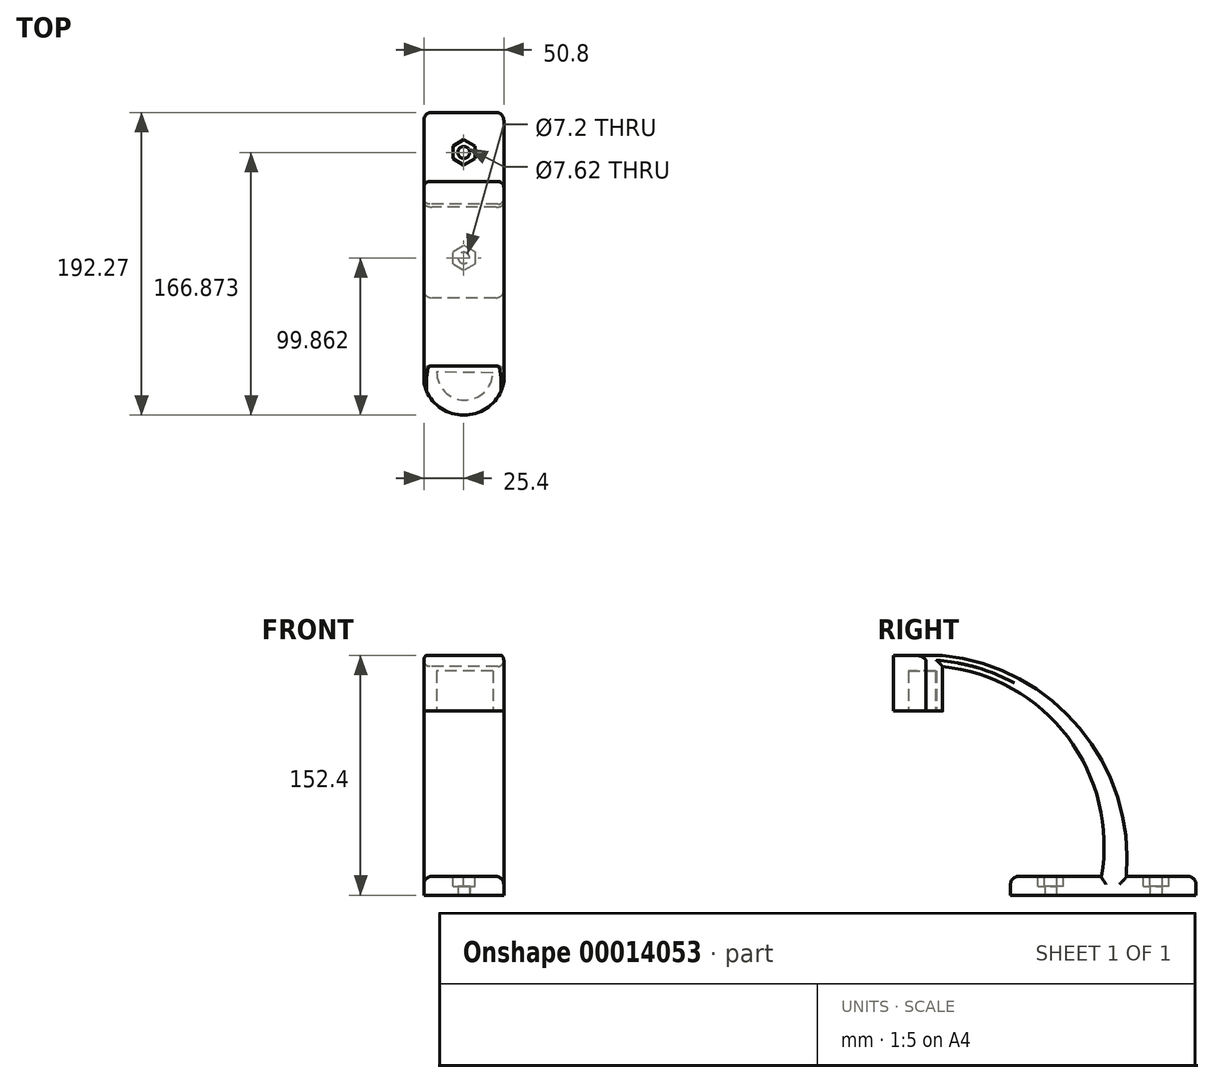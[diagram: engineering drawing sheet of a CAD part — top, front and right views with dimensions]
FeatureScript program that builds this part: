
annotation { "Feature Type Name" : "Feature", "Feature Type Description" : "" }
export const myFeature = defineFeature(function(context is Context, id is Id, definition is map)
    precondition{}
    {
        {
            var Q0;
            Q0=qCreatedBy(makeId("Right.planeOp"),FACE);
            var sketch = newSketch(context, id + "F0", { "sketchPlane" : qUnion([Q0])});
            skLineSegment(sketch, "E0.bottom", {"start": v(-57.77, 0) * mm, "end": v(60.04, 0) * mm});
            skLineSegment(sketch, "E0.top", {"start": v(-57.77, 11.91) * mm, "end": v(60.04, 11.91) * mm});
            skLineSegment(sketch, "E0.left", {"start": v(-57.77, 0) * mm, "end": v(-57.77, 11.91) * mm});
            skLineSegment(sketch, "E0.right", {"start": v(60.04, 0) * mm, "end": v(60.04, 11.91) * mm});
            skLineSegment(sketch, "E1.bottom", {"start": v(-132.44, 117) * mm, "end": v(-100.9, 117) * mm});
            skLineSegment(sketch, "E1.top", {"start": v(-132.44, 152.4) * mm, "end": v(-100.9, 152.4) * mm});
            skLineSegment(sketch, "E1.left", {"start": v(-132.44, 117) * mm, "end": v(-132.44, 152.4) * mm});
            skLineSegment(sketch, "E1.right", {"start": v(-100.9, 117) * mm, "end": v(-100.9, 152.4) * mm});
            skArc(sketch, "E2", {"start": v(15.8, 11.91) * mm, "mid": v(-13.86, 106) * mm, "end": v(-100.9, 152.4) * mm});
            skArc(sketch, "E3", {"start": v(0, 11.91) * mm, "mid": v(-21.52, 100.47) * mm, "end": v(-100.9, 145.2) * mm});
            skSolve(sketch);
        }
        {
            var Q0;
            Q0 = qSketchRegion(id + "F0", true);
            extrude(context, id + "F1", {"entities" : qUnion([Q0]), "depth" : 50.8 * mm});
        }
        {
            var Q0;
            Q0=makeQuery(id+"F1.opExtrude","SWEPT_FACE",FACE,{"disambiguationData":[OSD([sQuery(id+"F0.wireOp",EDGE,"E1.top")])]});
            var sketch = newSketch(context, id + "F2", { "sketchPlane" : qUnion([Q0])});
            skArc(sketch, "E4", {"start": v(0, -100.9) * mm, "mid": v(25.4, -132.23) * mm, "end": v(50.8, -100.9) * mm});
            skSolve(sketch);
        }
        {
            var Q0;
            {var subQ0=sQuery(id+"F0.wireOp",EDGE,"E1.top");var subQ4=makeQuery(id+"F1.opExtrude","SWEPT_EDGE",EDGE,{"disambiguationData":[OSD([subQ0,sQuery(id+"F0.wireOp",EDGE,"E1.left")])]});Q0=makeQuery(id+"F2.imprint","IMPRINT",FACE,{"disambiguationData":[TD([[makeQuery(id+"F2.imprint","IMPRINT",EDGE,{"derivedFrom":subQ4}),-1.0]])]});}
            extrude(context, id + "F3", {"entities" : qUnion([Q0]), "operationType" : NewBodyOperationType.REMOVE, "endBound" : BoundingType.UP_TO_NEXT, "oppositeDirection" : true, "depth" : 25.4 * mm});
        }
        {
            var Q0;
            Q0=makeQuery(id+"F1.opExtrude","CAP_EDGE",EDGE,{"disambiguationData":[OSD([sQuery(id+"F0.wireOp",EDGE,"E1.right")])],"isStart":false});
            var Q1;
            Q1=makeQuery(id+"F1.opExtrude","CAP_EDGE",EDGE,{"disambiguationData":[OSD([sQuery(id+"F0.wireOp",EDGE,"E1.right")])],"isStart":true});
            var Q2;
            Q2=makeQuery(id+"F1.opExtrude","CAP_EDGE",EDGE,{"disambiguationData":[OSD([sQuery(id+"F0.wireOp",EDGE,"E3")])],"isStart":false});
            var Q3;
            Q3=makeQuery(id+"F1.opExtrude","CAP_EDGE",EDGE,{"disambiguationData":[OSD([sQuery(id+"F0.wireOp",EDGE,"E2")])],"isStart":false});
            var Q4;
            Q4=makeQuery(id+"F3.boolean.opBoolean","COPY",EDGE,{"derivedFrom":makeQuery(id+"F3.opExtrude","CAP_EDGE",EDGE,{"disambiguationData":[OSD([sQuery(id+"F2.wireOp",EDGE,"E4")])],"isStart":false})});
            var Q5;
            Q5=makeQuery(id+"F1.opExtrude","CAP_EDGE",EDGE,{"disambiguationData":[OSD([sQuery(id+"F0.wireOp",EDGE,"E3")])],"isStart":true});
            var Q6;
            Q6=makeQuery(id+"F1.opExtrude","CAP_EDGE",EDGE,{"disambiguationData":[OSD([sQuery(id+"F0.wireOp",EDGE,"E2")])],"isStart":true});
            fillet(context, id + "F4", {"entities" : qUnion([Q0, Q1, Q2, Q3, Q4, Q5, Q6]), "radius" : 3.8 * mm, "tangentPropagation" : true, "allowEdgeOverflow" : false});
        }
        {
            var Q0;
            Q0=makeQuery(id+"F1.opExtrude","SWEPT_FACE",FACE,{"disambiguationData":[OSD([sQuery(id+"F0.wireOp",EDGE,"E1.bottom")])]});
            var sketch = newSketch(context, id + "F5", { "sketchPlane" : qUnion([Q0])});
            skArc(sketch, "E5", {"start": v(43.42, 100.9) * mm, "mid": v(26.02, 122.66) * mm, "end": v(8.61, 100.9) * mm});
            skLineSegment(sketch, "E6", {"start": v(43.84, 105.46) * mm, "end": v(8.18, 104.82) * mm});
            skSolve(sketch);
        }
        {
            var Q0;
            {var subQ0=sQuery(id+"F5.wireOp",EDGE,"E6");Q0=makeQuery(id+"F5.imprint","IMPRINT",FACE,{"disambiguationData":[TD([[makeQuery(id+"F5.imprint","IMPRINT",EDGE,{"derivedFrom":subQ0}),-1.0]])]});}
            extrude(context, id + "F6", {"entities" : qUnion([Q0]), "operationType" : NewBodyOperationType.REMOVE, "oppositeDirection" : true, "depth" : 25.4 * mm});
        }
        {
            var Q0;
            {var subQ0=sQuery(id+"F0.wireOp",EDGE,"E0.top");Q0=makeQuery(id+"F1.opExtrude","SWEPT_FACE",FACE,{"disambiguationData":[OSD([subQ0]),TDD([makeQuery(id+"F0.imprint","IMPRINT",EDGE,{"disambiguationData":[TD([[makeQuery(id+"F0.imprint","INTERSECT",VERTEX,{"derivedFrom":[subQ0,sQuery(id+"F0.wireOp",EDGE,"E0.left")]}),-1.0]])],"derivedFrom":subQ0})])]});}
            var sketch = newSketch(context, id + "F7", { "sketchPlane" : qUnion([Q0])});
            skCircle(sketch, "E7.cCircle", {"center": v(25.4, -32.37) * mm, "radius": 6.99 * mm, "construction": true});
            skLineSegment(sketch, "E7.0", {"start": v(32.39, -28.33) * mm, "end": v(32.39, -36.4) * mm});
            skLineSegment(sketch, "E7.1", {"start": v(32.39, -36.4) * mm, "end": v(25.4, -40.43) * mm});
            skLineSegment(sketch, "E7.2", {"start": v(25.4, -40.43) * mm, "end": v(18.41, -36.4) * mm});
            skLineSegment(sketch, "E7.3", {"start": v(18.41, -36.4) * mm, "end": v(18.41, -28.33) * mm});
            skLineSegment(sketch, "E7.4", {"start": v(18.41, -28.33) * mm, "end": v(25.4, -24.3) * mm});
            skLineSegment(sketch, "E7.5", {"start": v(25.4, -24.3) * mm, "end": v(32.39, -28.33) * mm});
            skPoint(sketch, "E7.0.midPoint", {"position": v(32.39, -32.37) * mm});
            skSolve(sketch);
        }
        {
            var Q0;
            {var subQ0=sQuery(id+"F0.wireOp",EDGE,"E0.top");Q0=makeQuery(id+"F1.opExtrude","SWEPT_FACE",FACE,{"disambiguationData":[OSD([subQ0]),TDD([makeQuery(id+"F0.imprint","IMPRINT",EDGE,{"disambiguationData":[TD([[makeQuery(id+"F0.imprint","INTERSECT",VERTEX,{"derivedFrom":[subQ0,sQuery(id+"F0.wireOp",EDGE,"E0.right")]}),1.0]])],"derivedFrom":subQ0})])]});}
            var sketch = newSketch(context, id + "F8", { "sketchPlane" : qUnion([Q0])});
            skCircle(sketch, "E8.cCircle", {"center": v(25.4, 34.64) * mm, "radius": 6.98 * mm, "construction": true});
            skLineSegment(sketch, "E8.0", {"start": v(32.38, 38.68) * mm, "end": v(32.38, 30.6) * mm});
            skLineSegment(sketch, "E8.1", {"start": v(32.39, 30.6) * mm, "end": v(25.4, 26.58) * mm});
            skLineSegment(sketch, "E8.2", {"start": v(25.4, 26.58) * mm, "end": v(18.41, 30.6) * mm});
            skLineSegment(sketch, "E8.3", {"start": v(18.41, 30.6) * mm, "end": v(18.41, 38.68) * mm});
            skLineSegment(sketch, "E8.4", {"start": v(18.41, 38.68) * mm, "end": v(25.4, 42.7) * mm});
            skLineSegment(sketch, "E8.5", {"start": v(25.4, 42.7) * mm, "end": v(32.38, 38.68) * mm});
            skPoint(sketch, "E8.0.midPoint", {"position": v(32.38, 34.64) * mm});
            skSolve(sketch);
        }
        {
            var Q0;
            Q0=makeQuery(id+"F7.imprint","IMPRINT",FACE,{"disambiguationData":[TD([[makeQuery(id+"F7.imprint","IMPRINT",EDGE,{"derivedFrom":sQuery(id+"F7.wireOp",EDGE,"E7.0")}),-1.0]])]});
            var Q1;
            Q1=makeQuery(id+"F8.imprint","IMPRINT",FACE,{"disambiguationData":[TD([[makeQuery(id+"F8.imprint","IMPRINT",EDGE,{"derivedFrom":sQuery(id+"F8.wireOp",EDGE,"E8.0")}),-1.0]])]});
            extrude(context, id + "F9", {"entities" : qUnion([Q0, Q1]), "operationType" : NewBodyOperationType.REMOVE, "oppositeDirection" : true, "depth" : 6.35 * mm});
        }
        {
            var Q0;
            Q0=makeQuery(id+"F1.opExtrude","CAP_EDGE",EDGE,{"disambiguationData":[OSD([sQuery(id+"F0.wireOp",EDGE,"E0.right")])],"isStart":false});
            var Q1;
            Q1=makeQuery(id+"F1.opExtrude","CAP_EDGE",EDGE,{"disambiguationData":[OSD([sQuery(id+"F0.wireOp",EDGE,"E0.left")])],"isStart":false});
            var Q2;
            Q2=makeQuery(id+"F1.opExtrude","CAP_EDGE",EDGE,{"disambiguationData":[OSD([sQuery(id+"F0.wireOp",EDGE,"E0.right")])],"isStart":true});
            var Q3;
            Q3=makeQuery(id+"F1.opExtrude","CAP_EDGE",EDGE,{"disambiguationData":[OSD([sQuery(id+"F0.wireOp",EDGE,"E0.left")])],"isStart":true});
            var Q4;
            {var subQ0=sQuery(id+"F0.wireOp",EDGE,"E0.top");Q4=makeQuery(id+"F1.opExtrude","CAP_EDGE",EDGE,{"disambiguationData":[OSD([subQ0]),TDD([makeQuery(id+"F0.imprint","IMPRINT",EDGE,{"disambiguationData":[TD([[makeQuery(id+"F0.imprint","INTERSECT",VERTEX,{"derivedFrom":[subQ0,sQuery(id+"F0.wireOp",EDGE,"E0.right")]}),1.0]])],"derivedFrom":subQ0})])],"isStart":true});}
            var Q5;
            {var subQ0=sQuery(id+"F0.wireOp",EDGE,"E0.top");Q5=makeQuery(id+"F1.opExtrude","CAP_EDGE",EDGE,{"disambiguationData":[OSD([subQ0]),TDD([makeQuery(id+"F0.imprint","IMPRINT",EDGE,{"disambiguationData":[TD([[makeQuery(id+"F0.imprint","INTERSECT",VERTEX,{"derivedFrom":[subQ0,sQuery(id+"F0.wireOp",EDGE,"E0.left")]}),-1.0]])],"derivedFrom":subQ0})])],"isStart":true});}
            var Q6;
            {var subQ0=sQuery(id+"F0.wireOp",EDGE,"E0.top");Q6=makeQuery(id+"F1.opExtrude","CAP_EDGE",EDGE,{"disambiguationData":[OSD([subQ0]),TDD([makeQuery(id+"F0.imprint","IMPRINT",EDGE,{"disambiguationData":[TD([[makeQuery(id+"F0.imprint","INTERSECT",VERTEX,{"derivedFrom":[subQ0,sQuery(id+"F0.wireOp",EDGE,"E0.right")]}),1.0]])],"derivedFrom":subQ0})])],"isStart":false});}
            var Q7;
            {var subQ0=sQuery(id+"F0.wireOp",EDGE,"E0.top");Q7=makeQuery(id+"F1.opExtrude","CAP_EDGE",EDGE,{"disambiguationData":[OSD([subQ0]),TDD([makeQuery(id+"F0.imprint","IMPRINT",EDGE,{"disambiguationData":[TD([[makeQuery(id+"F0.imprint","INTERSECT",VERTEX,{"derivedFrom":[subQ0,sQuery(id+"F0.wireOp",EDGE,"E0.left")]}),-1.0]])],"derivedFrom":subQ0})])],"isStart":false});}
            var Q8;
            Q8=makeQuery(id+"F1.opExtrude","SWEPT_EDGE",EDGE,{"disambiguationData":[OSD([sQuery(id+"F0.wireOp",EDGE,"E0.top"),sQuery(id+"F0.wireOp",EDGE,"E0.left")])]});
            var Q9;
            Q9=makeQuery(id+"F1.opExtrude","SWEPT_EDGE",EDGE,{"disambiguationData":[OSD([sQuery(id+"F0.wireOp",EDGE,"E0.top"),sQuery(id+"F0.wireOp",EDGE,"E0.right")])]});
            fillet(context, id + "F10", {"entities" : qUnion([Q0, Q1, Q2, Q3, Q4, Q5, Q6, Q7, Q8, Q9]), "radius" : 5.08 * mm, "tangentPropagation" : true, "allowEdgeOverflow" : false});
        }
        {
            var Q0;
            Q0=makeQuery(id+"F1.opExtrude","SWEPT_FACE",FACE,{"disambiguationData":[OSD([sQuery(id+"F0.wireOp",EDGE,"E0.bottom")])]});
            var sketch = newSketch(context, id + "F11", { "sketchPlane" : qUnion([Q0])});
            skCircle(sketch, "E9", {"center": v(25.4, 32.37) * mm, "radius": 3.6 * mm});
            skCircle(sketch, "E10", {"center": v(25.4, -34.64) * mm, "radius": 3.81 * mm});
            skSolve(sketch);
        }
        {
            var Q0;
            Q0=makeQuery(id+"F11.imprint","IMPRINT",FACE,{"disambiguationData":[TD([[makeQuery(id+"F11.imprint","IMPRINT",EDGE,{"derivedFrom":sQuery(id+"F11.wireOp",EDGE,"E10")}),1.0]])]});
            var Q1;
            Q1=makeQuery(id+"F11.imprint","IMPRINT",FACE,{"disambiguationData":[TD([[makeQuery(id+"F11.imprint","IMPRINT",EDGE,{"derivedFrom":sQuery(id+"F11.wireOp",EDGE,"E9")}),1.0]])]});
            extrude(context, id + "F12", {"entities" : qUnion([Q0, Q1]), "operationType" : NewBodyOperationType.REMOVE, "endBound" : BoundingType.UP_TO_NEXT, "oppositeDirection" : true, "depth" : 25.4 * mm});
        }
    });
